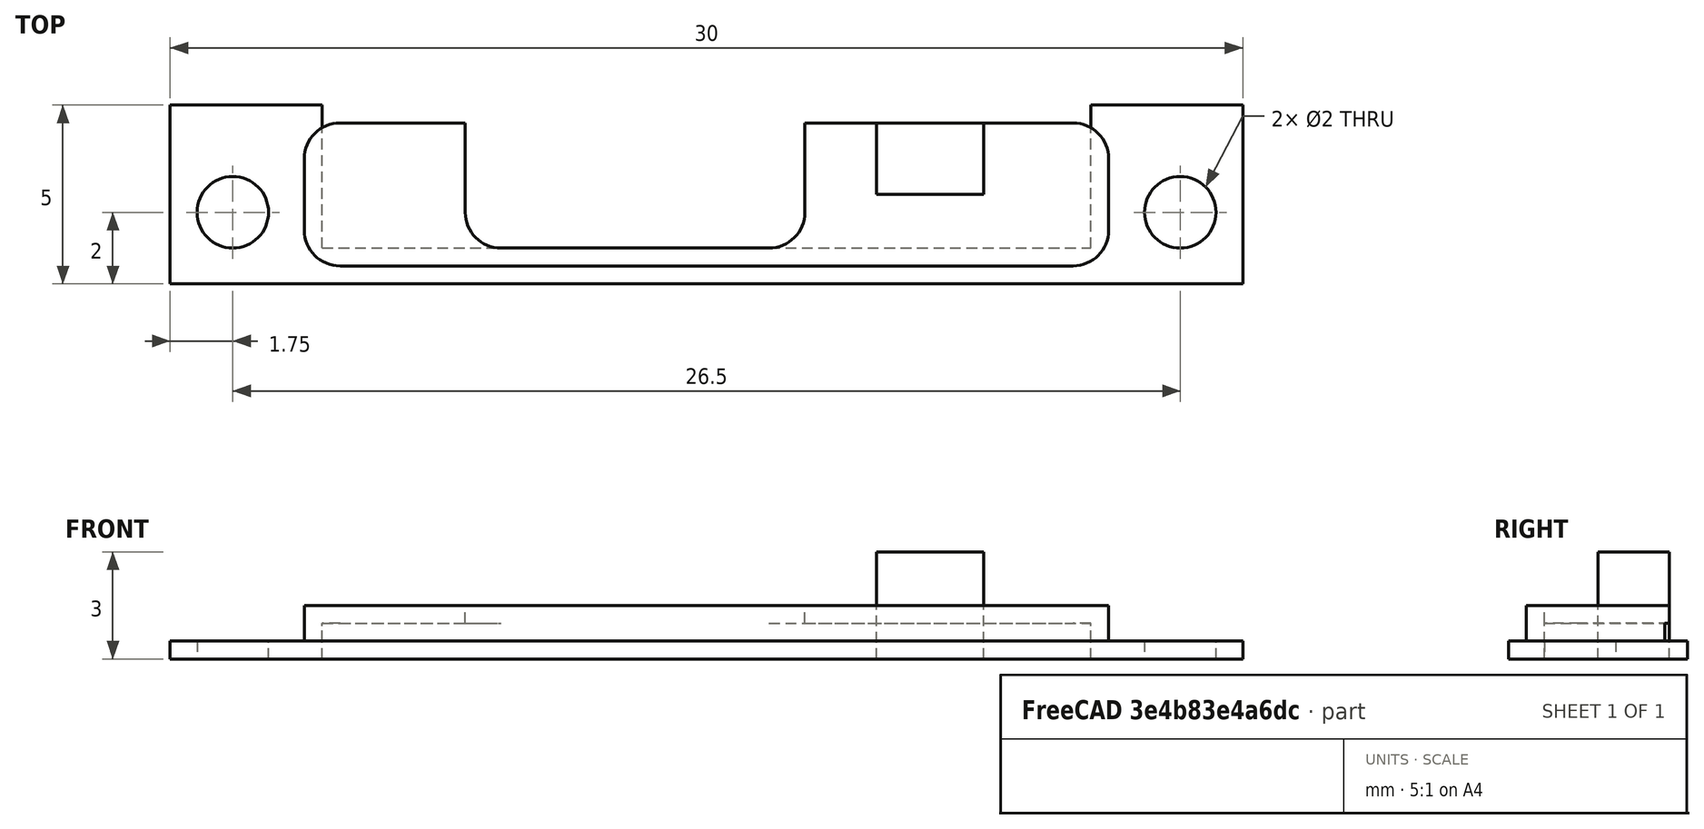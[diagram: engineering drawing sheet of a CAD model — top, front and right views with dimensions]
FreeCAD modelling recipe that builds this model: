
FCSTD DOCUMENT  (FreeCAD 0.20R29603 (Git))
Label: ipod_usb_c
License: All rights reserved
LicenseURL: http://en.wikipedia.org/wiki/All_rights_reserved
objects: Part::Box×5, Part::Cut×3, Part::Cylinder×2, Part::MultiFuse×2, Part::Fillet×2
note: 14 computed .brp shape members not serialized (recipe doc carries the construction recipe); baked Part::Feature solids carry a one-line shape summary decoded from their .brp

FEATURE [Part::Cylinder] Cylinder
  Angle = 360
  AttacherType = Attacher::AttachEngine3D
  FirstAngle = 0
  Height = 10
  Placement = pos=(1.75,2,0) rot=(0,0,1;0rad)
  Radius = 1
  SecondAngle = 0
FEATURE [Part::Cylinder] Cylinder001
  Angle = 360
  AttacherType = Attacher::AttachEngine3D
  FirstAngle = 0
  Height = 10
  Placement = pos=(28.25,2,0) rot=(0,0,1;0rad)
  Radius = 1
  SecondAngle = 0
FEATURE [Part::Box] Box001  label="Cube001"
  AttacherType = Attacher::AttachEngine3D
  Height = 1
  Length = 22.5
  Placement = pos=(3.75,0.5,0.5) rot=(0,0,1;0rad)
  Width = 4
FEATURE [Part::MultiFuse] Fusion
  Shapes = -> [Cylinder001,Cylinder]
FEATURE [Part::Box] Box002  label="Cube002(usb_c)"
  AttacherType = Attacher::AttachEngine3D
  Height = 1.5
  Length = 9.5
  Placement = pos=(8.25,1,0) rot=(0,0,1;0rad)
  Width = 3.5
FEATURE [Part::Box] Box003  label="Cube003(switch)"
  AttacherType = Attacher::AttachEngine3D
  Height = 3
  Length = 3
  Placement = pos=(19.75,2.5,0) rot=(0,0,1;0rad)
  Width = 2
FEATURE [Part::Box] Box  label="Cube(backing)"
  AttacherType = Attacher::AttachEngine3D
  Height = 0.5
  Length = 30
  Width = 5
FEATURE [Part::Box] Box004  label="Cube002(back_cutter)"
  AttacherType = Attacher::AttachEngine3D
  Height = 1
  Length = 21.5
  Placement = pos=(4.25,1,0) rot=(0,0,1;0rad)
  Width = 4
FEATURE [Part::Fillet] Fillet
  Base = -> Box001
  Edges = 4 edges r=1: [Edge1,Edge3,Edge5,Edge7]
FEATURE [Part::MultiFuse] Fusion003
  Shapes = -> [Fillet,Box]
FEATURE [Part::Cut] Cut
  Base = -> Fusion003
  Tool = -> Fusion
FEATURE [Part::Fillet] Fillet001
  Base = -> Box002
  Edges = 2 edges r=1: [Edge1,Edge5]
FEATURE [Part::Cut] Cut001
  Base = -> Cut
  Tool = -> Fillet001
FEATURE [Part::Cut] Cut002
  Base = -> Cut001
  Tool = -> Box004
